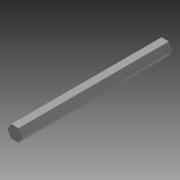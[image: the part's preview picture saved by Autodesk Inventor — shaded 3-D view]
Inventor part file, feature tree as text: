
AUTODESK INVENTOR PART (.ipt)
format: ipt  version: 2014 (Build 180170000, 170)  size: 92,160 bytes
history: native  units: in
note: dims shown in document units (in); Inventor stores cm internally (conversion verified against a paired STEP export)
features: extrude x1, sketch x1
ambient origin geometry x8: Origin, YZ Plane, XZ Plane, XY Plane, X Axis, Y Axis, Z Axis, Center Point
bodies: Solid1 (feature_tree)
feature tree (2):
  extrude  "Extrusion1"  Depth=6.0in TaperAngle=0.0deg
  sketch  "Sketch1"  dims[d0=0.5in d1=6.0in d2=0.0in]
